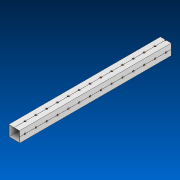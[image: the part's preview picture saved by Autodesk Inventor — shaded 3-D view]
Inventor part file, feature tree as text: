
AUTODESK INVENTOR PART (.ipt)
format: ipt  version: 2022.2 (Build 262287000, 287)  size: 756,224 bytes
history: native  units: in
note: dims shown in document units (in); Inventor stores cm internally (conversion verified against a paired STEP export)
features: other x28, pattern_linear x2, extrude x1, sketch x1
ambient origin geometry x8: Origin, YZ Plane, XZ Plane, XY Plane, X Axis, Y Axis, Z Axis, Center Point
bodies: Solid1 (feature_tree)
feature tree (32):
  extrude  "Extrusion1"  TaperAngle=0.0deg  [1 undecoded]
  other  "Work Axis1"
  other  "Work Axis2"
  pattern_linear  "Rectangular Pattern1"  Count1=14  [1 undecoded]
  pattern_linear  "Rectangular Pattern2"  Spacing1=1.0in  [1 undecoded]
  sketch  "Sketch1"  dims[d0=45.0in d1=0.0in d2=5.5118in d4=1.0in d5=5.1181in d7=1.0in]
  other  "Work Axis3"
  other  "Work Axis4"
  other  "Work Axis5"
  other  "Work Axis6"
  other  "Work Axis7"
  other  "Work Axis8"
  other  "Work Axis9"
  other  "Work Axis10"
  other  "Work Axis11"
  other  "Work Axis12"
  other  "Work Axis13"
  other  "Work Axis14"
  other  "Work Axis15"
  other  "Work Axis16"
  other  "Work Axis17"
  other  "Work Axis63"
  other  "Work Axis64"
  other  "Work Axis65"
  other  "Work Axis66"
  other  "Work Axis67"
  other  "Work Axis68"
  other  "Work Axis69"
  other  "Work Axis70"
  other  "Work Axis71"
  other  "Work Axis72"
  other  "LPattern2"
note: 3 required parameter values undecoded (feature->parameter linkage not recoverable at this tier; creation-order binding heuristic only, values carry confidence <= 0.55)
